# Revit family: STYLUS BASIS 1500FS BATH OVERFLOW
name_source: partatom
category: Plumbing Fixtures
units: mm (PartAtom-declared; Revit-internal decimal feet)

## family parameters
Cut with Voids When Loaded = Yes
Host = Face
OmniClass Number = 23.45.05.14.21
OmniClass Title = Bathtubs
Part Type = Normal
Room Calculation Point = No
Round Connector Dimension = Use Diameter
Shared = No

## types (1)
- STYLUS BASIS 1500FS BATH OVERFLOW
    Assembly Code = D2010510
    CW Connection = No
    Default Elevation = 0 mm  [stored 0 ft]
    Description = STYLUS BASIS 1500FS BATH OVERFLOW
    HW Connection = No
    Manufacturer = GWA Bathrooms & Kitchens
    Material_Bath = GWA-Acrylic-White
    Material_Waste = GWA-Metalwork-White
    Model = BB5FWOF
    URL = https://www.caroma.com.au
    Vent Connection = No
    Waste Connection = Yes

note: [stored X ft] marks values corroborated as IEEE doubles in the binary element streams (Revit-internal decimal feet)

## geometry (parser evidence)
native form markers: Sweep x2
no freeform markers — native parametric forms only
